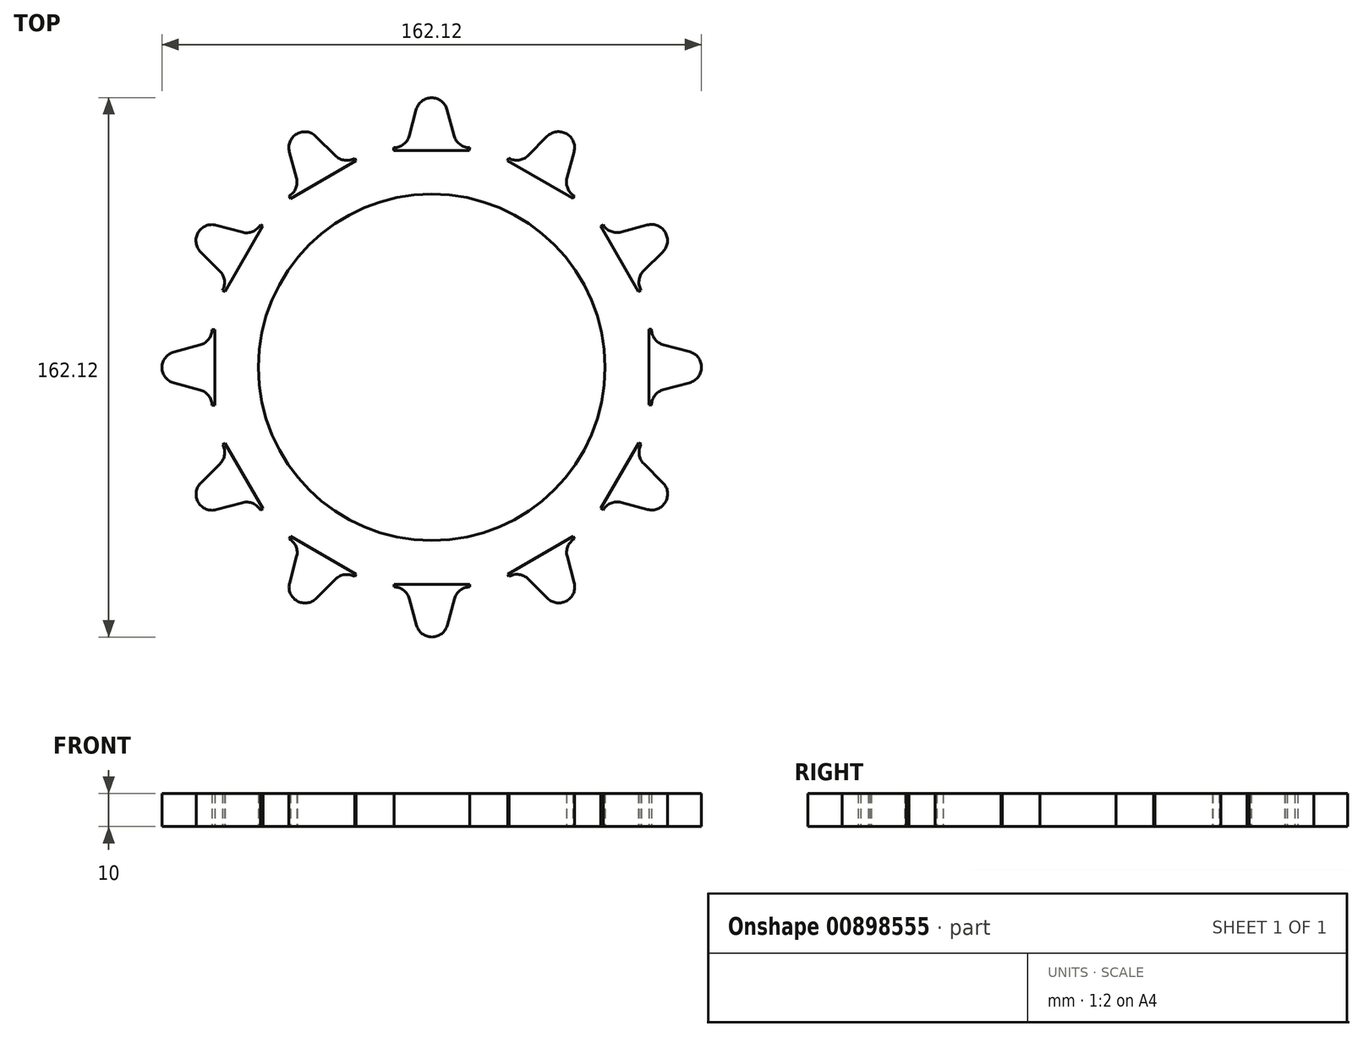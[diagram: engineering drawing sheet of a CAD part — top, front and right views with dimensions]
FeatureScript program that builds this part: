
annotation { "Feature Type Name" : "Feature", "Feature Type Description" : "" }
export const myFeature = defineFeature(function(context is Context, id is Id, definition is map)
    precondition{}
    {
        {
            var Q0;
            Q0=qCreatedBy(makeId("Top.planeOp"),FACE);
            var sketch = newSketch(context, id + "F0", { "sketchPlane" : qUnion([Q0])});
            skArc(sketch, "E0", {"start": v(-4.6, -77.5) * mm, "mid": v(0.04, -81.06) * mm, "end": v(4.67, -77.5) * mm});
            skLineSegment(sketch, "E1.MirrorCS", {"start": v(4.67, -77.5) * mm, "end": v(6.79, -69.6) * mm});
            skPoint(sketch, "E2.end.orphan", {"position": v(0.04, -81.06) * mm});
            skLineSegment(sketch, "E3", {"start": v(0.04, -76.26) * mm, "end": v(0.04, -48.9) * mm, "construction": true});
            skArc(sketch, "E4", {"start": v(11.43, -66.04) * mm, "mid": v(8.5, -67.03) * mm, "end": v(6.79, -69.6) * mm});
            skLineSegment(sketch, "E5.MirrorCS", {"start": v(-4.6, -77.5) * mm, "end": v(-6.72, -69.6) * mm});
            skArc(sketch, "E6.MirrorCS", {"start": v(-11.35, -66.04) * mm, "mid": v(-8.43, -67.03) * mm, "end": v(-6.72, -69.6) * mm});
            skLineSegment(sketch, "E7", {"start": v(11.43, -66.04) * mm, "end": v(11.43, -65.2) * mm});
            skLineSegment(sketch, "E8", {"start": v(11.43, -65.2) * mm, "end": v(-11.33, -65.2) * mm});
            skLineSegment(sketch, "E9", {"start": v(-11.33, -65.2) * mm, "end": v(-11.35, -66.04) * mm});
            skSolve(sketch);
        }
        {
            var Q0;
            Q0=makeQuery(id+"F0.imprint","IMPRINT",FACE,{"disambiguationData":[TD([[makeQuery(id+"F0.imprint","IMPRINT",EDGE,{"derivedFrom":sQuery(id+"F0.wireOp",EDGE,"E0")}),1.0]])]});
            extrude(context, id + "F1", {"entities" : qUnion([Q0]), "depth" : 10 * mm, "offsetDistance" : 25 * mm});
        }
        {
            var Q0;
            Q0=qCreatedBy(makeId("Top.planeOp"),FACE);
            var sketch = newSketch(context, id + "F2", { "sketchPlane" : qUnion([Q0])});
            skCircle(sketch, "E10", {"center": v(0, 0) * mm, "radius": 80.95 * mm});
            skSolve(sketch);
        }
        {
            var Q0;
            Q0=makeQuery(id+"F1.opExtrude","SWEPT_BODY",BODY,{"disambiguationData":[OSD([sQuery(id+"F0.wireOp",EDGE,"E0"),sQuery(id+"F0.wireOp",EDGE,"262573bb-3e77-4354-b6c7-9d77f2da6c65"),sQuery(id+"F0.wireOp",EDGE,"E1.MirrorCS"),sQuery(id+"F0.wireOp",EDGE,"c846a7f2-ef41-490e-a8bc-b35fb695e2b9"),sQuery(id+"F0.wireOp",EDGE,"2e5b6cda-26f7-4d04-b22e-83611f81f709.MirrorCS"),sQuery(id+"F0.wireOp",EDGE,"7539efcd-568e-4399-94fe-b33773e1d73a"),sQuery(id+"F0.wireOp",EDGE,"71e96a4c-d4a5-49d9-ab2a-2f2079ea32e9"),sQuery(id+"F0.wireOp",EDGE,"c15741b3-808f-4f5e-8203-5713ff1f5864")])]});
            var Q1;
            Q1=sQuery(id+"F2.wireOp",EDGE,"E10");
            circularPattern(context, id + "F3", {"operationType" : NewBodyOperationType.ADD, "entities" : qUnion([Q0]), "axis" : qUnion([Q1]), "angle" : 360 * degree, "instanceCount" : 12, "equalSpace" : true});
        }
        {
            var Q0;
            Q0=qCreatedBy(makeId("Top.planeOp"),FACE);
            var sketch = newSketch(context, id + "F4", { "sketchPlane" : qUnion([Q0])});
            skCircle(sketch, "E11", {"center": v(0, 0) * mm, "radius": 52.09 * mm});
            skSolve(sketch);
        }
        {
            var Q0;
            Q0=makeQuery(id+"F4.imprint","IMPRINT",FACE,{"disambiguationData":[TD([[makeQuery(id+"F4.imprint","IMPRINT",EDGE,{"derivedFrom":sQuery(id+"F4.wireOp",EDGE,"E11")}),1.0]])]});
            extrude(context, id + "F5", {"entities" : qUnion([Q0]), "operationType" : NewBodyOperationType.ADD, "depth" : 10 * mm, "offsetDistance" : 25 * mm});
        }
    });
